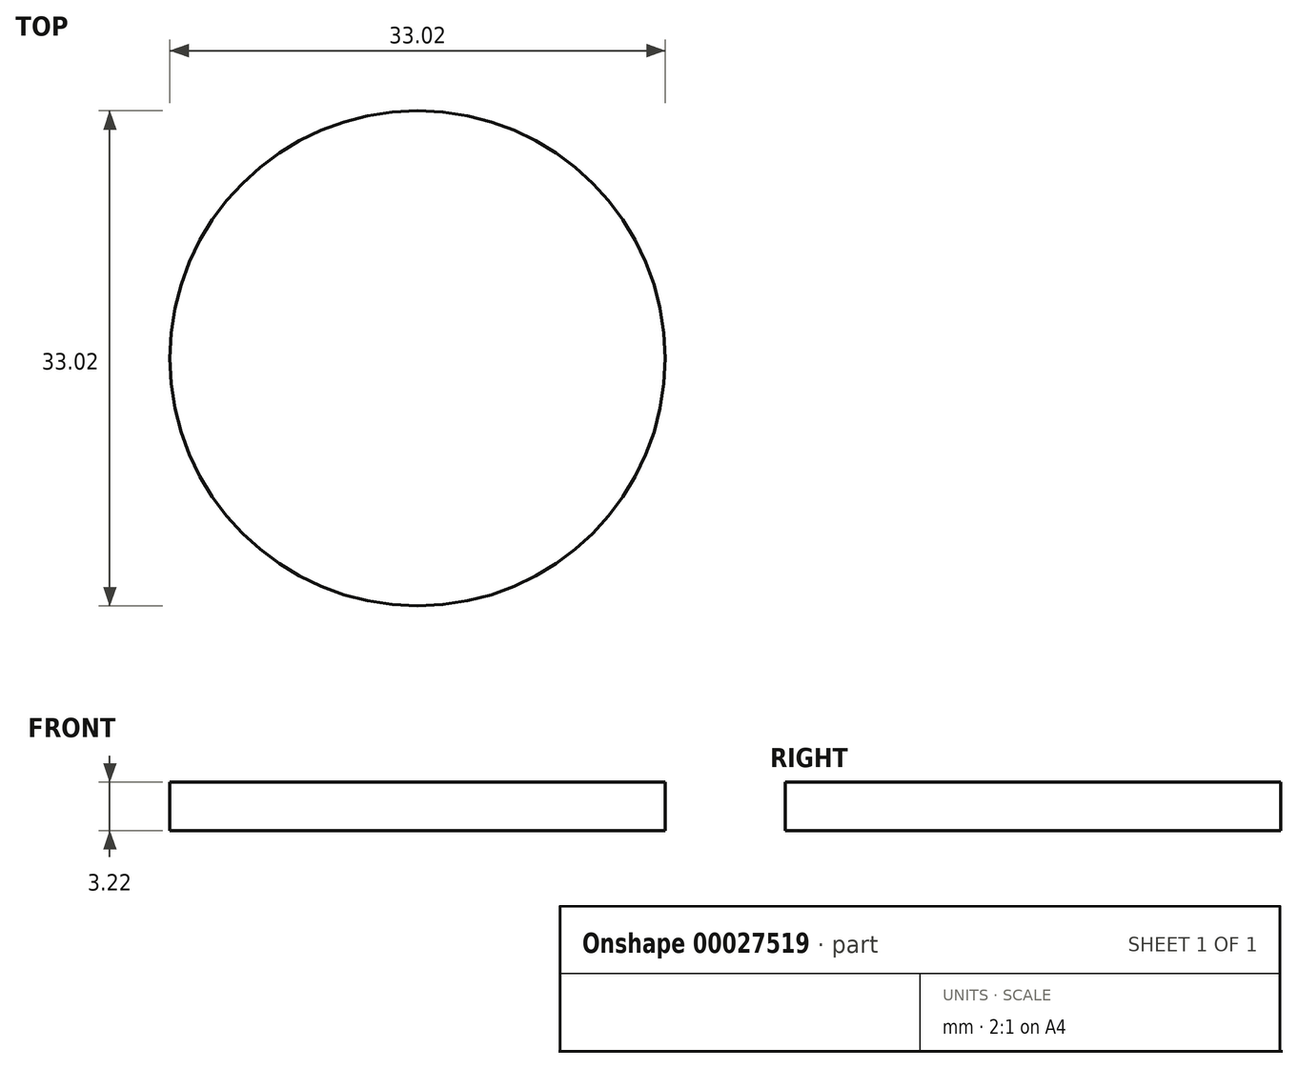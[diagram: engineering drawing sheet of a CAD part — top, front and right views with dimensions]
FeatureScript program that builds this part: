
annotation { "Feature Type Name" : "Feature", "Feature Type Description" : "" }
export const myFeature = defineFeature(function(context is Context, id is Id, definition is map)
    precondition{}
    {
        {
            var Q0;
            Q0=qCreatedBy(makeId("Top.planeOp"),FACE);
            var sketch = newSketch(context, id + "F0", { "sketchPlane" : qUnion([Q0])});
            skCircle(sketch, "E0", {"center": v(0, 0) * mm, "radius": 16.5 * mm});
            skSolve(sketch);
        }
        {
            var Q0;
            Q0=sQuery(id+"F0.wireOp",EDGE,"E0");
            extrude(context, id + "F1", {"bodyType" : ToolBodyType.SURFACE, "surfaceEntities" : qUnion([Q0]), "depth" : 3.22 * mm});
        }
    });
